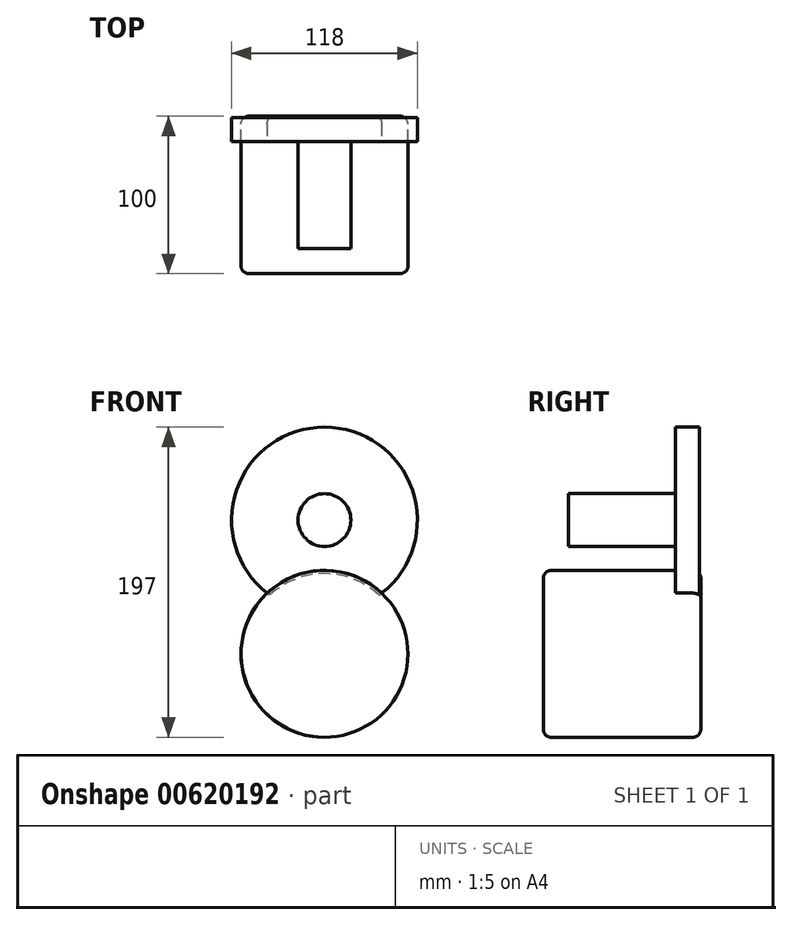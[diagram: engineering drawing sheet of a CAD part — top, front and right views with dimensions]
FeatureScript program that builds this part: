
annotation { "Feature Type Name" : "Feature", "Feature Type Description" : "" }
export const myFeature = defineFeature(function(context is Context, id is Id, definition is map)
    precondition{}
    {
        {
            var Q0;
            Q0=qCreatedBy(makeId("Front.planeOp"),FACE);
            var sketch = newSketch(context, id + "F0", { "sketchPlane" : qUnion([Q0])});
            skCircle(sketch, "E0", {"center": v(0, 0) * mm, "radius": 105 * mm});
            skSolve(sketch);
        }
        {
            var Q0;
            Q0=qCreatedBy(makeId("Front.planeOp"),FACE);
            var sketch = newSketch(context, id + "F1", { "sketchPlane" : qUnion([Q0])});
            skCircle(sketch, "E1", {"center": v(0, -85) * mm, "radius": 53 * mm});
            skSolve(sketch);
        }
        {
            var Q0;
            Q0 = qSketchRegion(id + "F1", true);
            extrude(context, id + "F2", {"entities" : qUnion([Q0]), "depth" : 100 * mm, "offsetDistance" : 25 * mm, "symmetric" : true});
        }
        {
            var Q0;
            Q0=makeQuery(id+"F2.opExtrude","CAP_EDGE",EDGE,{"disambiguationData":[OSD([sQuery(id+"F1.wireOp",EDGE,"E1")])],"isStart":false});
            var Q1;
            Q1=makeQuery(id+"F2.opExtrude","CAP_EDGE",EDGE,{"disambiguationData":[OSD([sQuery(id+"F1.wireOp",EDGE,"E1")])],"isStart":true});
            fillet(context, id + "F3", {"entities" : qUnion([Q0, Q1]), "radius" : 5 * mm, "tangentPropagation" : true, "allowEdgeOverflow" : false});
        }
        {
            var Q0;
            Q0=qCreatedBy(makeId("Front.planeOp"),FACE);
            var sketch = newSketch(context, id + "F4", { "sketchPlane" : qUnion([Q0])});
            skCircle(sketch, "E2", {"center": v(0, 0) * mm, "radius": 16.75 * mm});
            skSolve(sketch);
        }
        {
            var Q0;
            Q0 = qSketchRegion(id + "F4", true);
            extrude(context, id + "F5", {"entities" : qUnion([Q0]), "operationType" : NewBodyOperationType.ADD, "depth" : 68 * mm, "offsetDistance" : 25 * mm, "symmetric" : true});
        }
        {
            var Q0;
            Q0=makeQuery(id+"F5.opExtrude","CAP_FACE",FACE,{"disambiguationData":[OSD([sQuery(id+"F4.wireOp",EDGE,"E2")])],"isStart":true});
            var sketch = newSketch(context, id + "F6", { "sketchPlane" : qUnion([Q0])});
            skCircle(sketch, "E3", {"center": v(0, 0) * mm, "radius": 59 * mm});
            skSolve(sketch);
        }
        {
            var Q0;
            Q0 = qSketchRegion(id + "F6", true);
            extrude(context, id + "F7", {"entities" : qUnion([Q0]), "operationType" : NewBodyOperationType.ADD, "depth" : 15 * mm, "offsetDistance" : 25 * mm});
        }
    });
